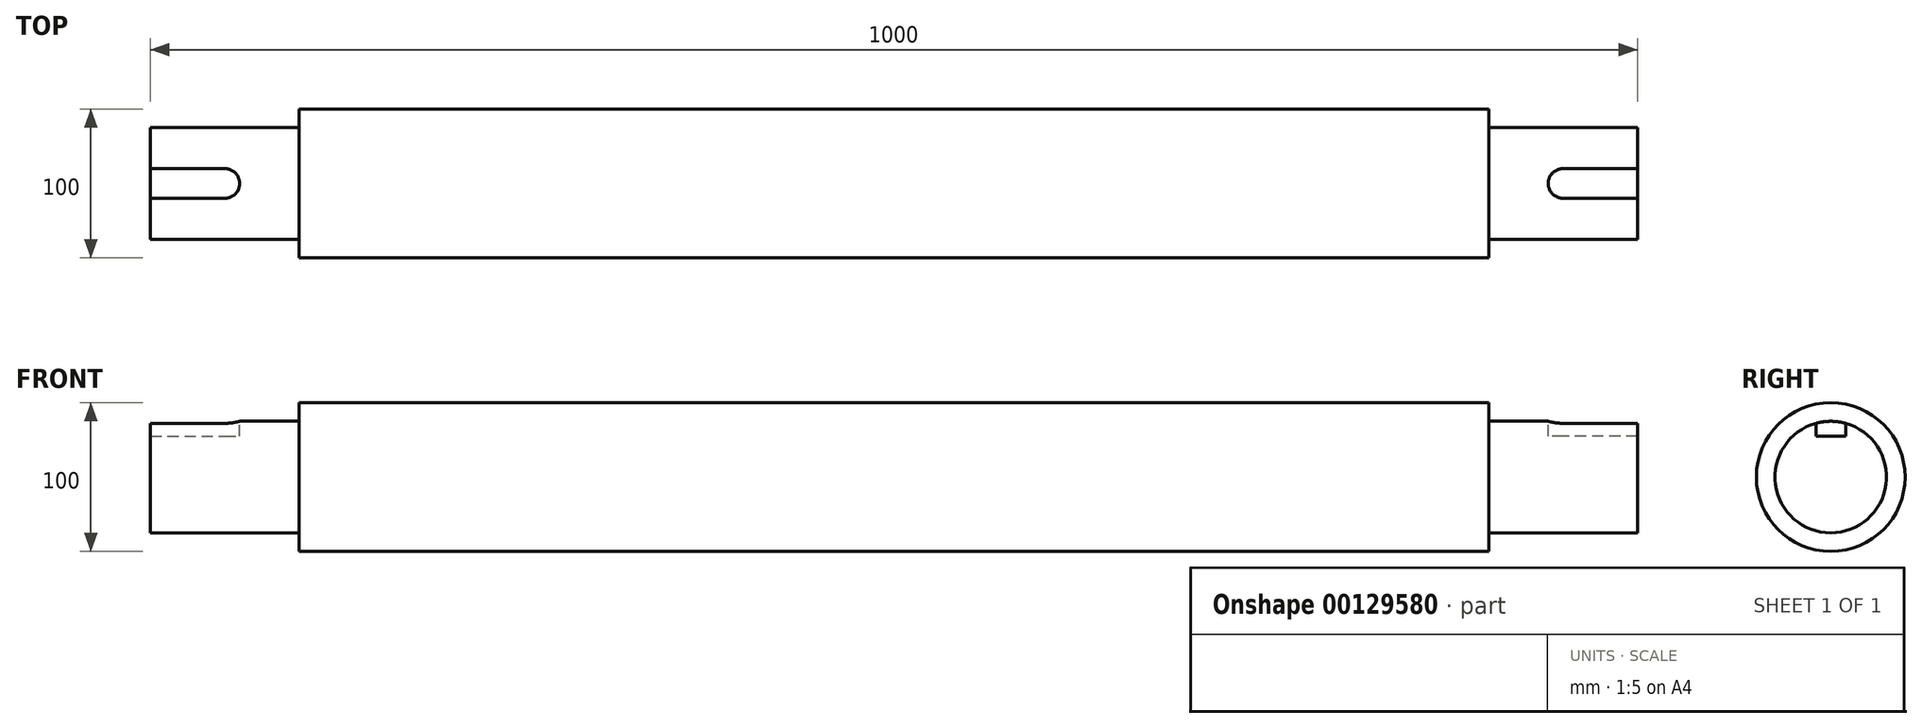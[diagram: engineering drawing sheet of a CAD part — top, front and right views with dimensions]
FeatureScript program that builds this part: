
annotation { "Feature Type Name" : "Feature", "Feature Type Description" : "" }
export const myFeature = defineFeature(function(context is Context, id is Id, definition is map)
    precondition{}
    {
        {
            var Q0;
            Q0=qCreatedBy(makeId("Front.planeOp"),FACE);
            var sketch = newSketch(context, id + "F0", { "sketchPlane" : qUnion([Q0])});
            skLineSegment(sketch, "E0", {"start": v(-500, 0) * mm, "end": v(500, 0) * mm});
            skLineSegment(sketch, "E1", {"start": v(-500, 0) * mm, "end": v(-500, 37.5) * mm});
            skLineSegment(sketch, "E2", {"start": v(-500, 37.5) * mm, "end": v(-400, 37.5) * mm});
            skLineSegment(sketch, "E3", {"start": v(-400, 37.5) * mm, "end": v(-400, 50) * mm});
            skLineSegment(sketch, "E4", {"start": v(-400, 50) * mm, "end": v(400, 50) * mm});
            skLineSegment(sketch, "E5", {"start": v(400, 50) * mm, "end": v(400, 37.5) * mm});
            skLineSegment(sketch, "E6", {"start": v(400, 37.5) * mm, "end": v(500, 37.5) * mm});
            skLineSegment(sketch, "E7", {"start": v(500, 37.5) * mm, "end": v(500, 0) * mm});
            skSolve(sketch);
        }
        {
            var Q0;
            Q0 = qSketchRegion(id + "F0", true);
            var Q1;
            Q1=sQuery(id+"F0.wireOp",EDGE,"E0");
            revolve(context, id + "F1", {"entities" : qUnion([Q0]), "axis" : qUnion([Q1]), "revolveType" : RevolveType.FULL});
        }
        {
            var Q0;
            Q0=qCreatedBy(makeId("Top.planeOp"),FACE);
            cPlane(context, id + "F2", {"entities" : qUnion([Q0]), "cplaneType" : CPlaneType.OFFSET, "offset" : (75 / 2) * mm, "width" : 150 * mm, "height" : 150 * mm});
        }
        {
            var Q0;
            Q0=qCreatedBy(id+"F2.planeOp",FACE);
            var sketch = newSketch(context, id + "F3", { "sketchPlane" : qUnion([Q0])});
            skLineSegment(sketch, "E8.bottom", {"start": v(-500, 10) * mm, "end": v(-450, 10) * mm});
            skLineSegment(sketch, "E8.top", {"start": v(-500, -10) * mm, "end": v(-450, -10) * mm});
            skLineSegment(sketch, "E8.left", {"start": v(-500, 10) * mm, "end": v(-500, -10) * mm});
            skArc(sketch, "E9", {"start": v(-450, -10) * mm, "mid": v(-440, 0) * mm, "end": v(-450, 10) * mm});
            skLineSegment(sketch, "E10", {"start": v(-450, 0) * mm, "end": v(0, 0) * mm, "construction": true});
            skPoint(sketch, "E10.endSnap0", {"position": v(-440, 0) * mm});
            skLineSegment(sketch, "E11", {"start": v(0, 10) * mm, "end": v(0, -10) * mm, "construction": true});
            skArc(sketch, "E12.MirrorCS", {"start": v(450, -10) * mm, "mid": v(440, 0) * mm, "end": v(450, 10) * mm});
            skLineSegment(sketch, "E13.MirrorCS", {"start": v(500, -10) * mm, "end": v(450, -10) * mm});
            skLineSegment(sketch, "E14.MirrorCS", {"start": v(500, 10) * mm, "end": v(450, 10) * mm});
            skLineSegment(sketch, "E15.MirrorCS", {"start": v(500, 10) * mm, "end": v(500, -10) * mm});
            skSolve(sketch);
        }
        {
            var Q0;
            Q0 = qSketchRegion(id + "F3", true);
            extrude(context, id + "F4", {"entities" : qUnion([Q0]), "operationType" : NewBodyOperationType.REMOVE, "oppositeDirection" : true, "depth" : 10 * mm});
        }
    });
